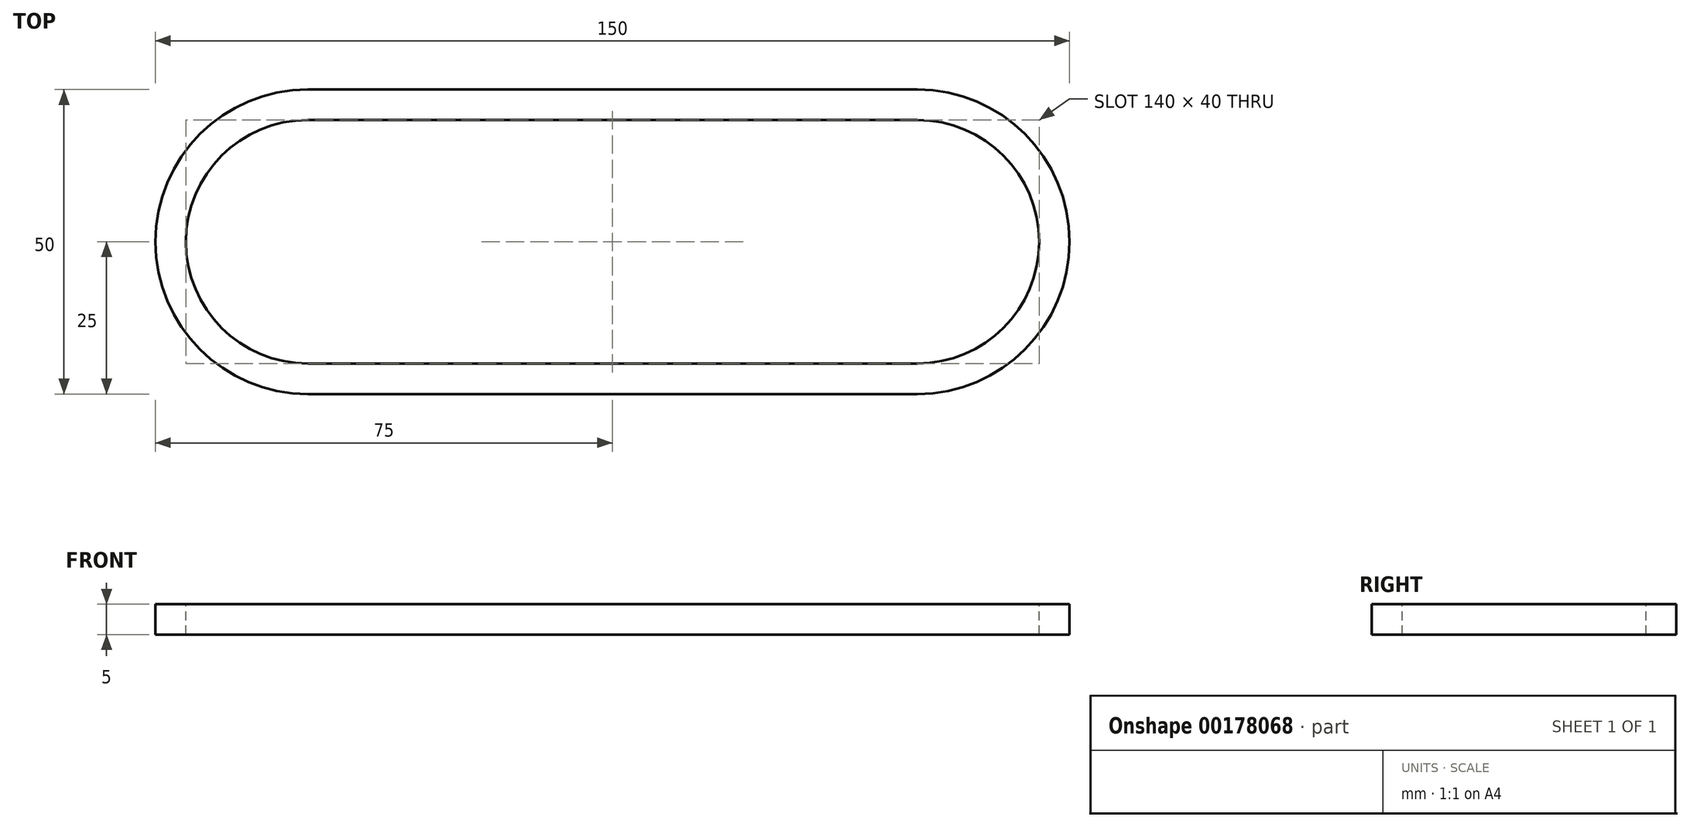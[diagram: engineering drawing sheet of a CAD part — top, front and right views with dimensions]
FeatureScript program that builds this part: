
annotation { "Feature Type Name" : "Feature", "Feature Type Description" : "" }
export const myFeature = defineFeature(function(context is Context, id is Id, definition is map)
    precondition{}
    {
        {
            var Q0;
            Q0=qCreatedBy(makeId("Top.planeOp"),FACE);
            var sketch = newSketch(context, id + "F0", { "sketchPlane" : qUnion([Q0])});
            skLineSegment(sketch, "E0", {"start": v(0, 0) * mm, "end": v(0, 25) * mm, "construction": true});
            skLineSegment(sketch, "E1", {"start": v(0, 0) * mm, "end": v(0, -25) * mm, "construction": true});
            skLineSegment(sketch, "E2", {"start": v(0, 25) * mm, "end": v(-50, 25) * mm});
            skLineSegment(sketch, "E3", {"start": v(0, -25) * mm, "end": v(-50, -25) * mm});
            skCircle(sketch, "E4", {"center": v(-50, 0) * mm, "radius": 25 * mm});
            skLineSegment(sketch, "E5.MirrorCS", {"start": v(0, 25) * mm, "end": v(50, 25) * mm});
            skCircle(sketch, "E6.MirrorC", {"center": v(50, 0) * mm, "radius": 25 * mm});
            skLineSegment(sketch, "E7.MirrorCS", {"start": v(0, -25) * mm, "end": v(50, -25) * mm});
            skSolve(sketch);
        }
        {
            var Q0;
            Q0 = qSketchRegion(id + "F0", true);
            extrude(context, id + "F1", {"entities" : qUnion([Q0]), "depth" : 5 * mm});
        }
        {
            var Q0;
            Q0=makeQuery(id+"F1.opExtrude","CAP_FACE",FACE,{"disambiguationData":[OSD([sQuery(id+"F0.wireOp",EDGE,"E2"),sQuery(id+"F0.wireOp",EDGE,"E3"),sQuery(id+"F0.wireOp",EDGE,"E4"),sQuery(id+"F0.wireOp",EDGE,"E5.MirrorCS"),sQuery(id+"F0.wireOp",EDGE,"E6.MirrorC"),sQuery(id+"F0.wireOp",EDGE,"E7.MirrorCS")])],"isStart":false});
            var sketch = newSketch(context, id + "F2", { "sketchPlane" : qUnion([Q0])});
            skLineSegment(sketch, "E8", {"start": v(0, 20) * mm, "end": v(0, -20) * mm, "construction": true});
            skLineSegment(sketch, "E9", {"start": v(0, 20) * mm, "end": v(-50, 20) * mm});
            skLineSegment(sketch, "E10", {"start": v(0, -20) * mm, "end": v(-50, -20) * mm});
            skCircle(sketch, "E11", {"center": v(-50, 0) * mm, "radius": 20 * mm});
            skLineSegment(sketch, "E12.MirrorCS", {"start": v(0, 20) * mm, "end": v(50, 20) * mm});
            skCircle(sketch, "E13.MirrorC", {"center": v(50, 0) * mm, "radius": 20 * mm});
            skLineSegment(sketch, "E14.MirrorCS", {"start": v(0, -20) * mm, "end": v(50, -20) * mm});
            skLineSegment(sketch, "E15", {"start": v(-50, 20) * mm, "end": v(-50, -20) * mm});
            skLineSegment(sketch, "E16", {"start": v(50, 20) * mm, "end": v(50, -20) * mm});
            skSolve(sketch);
        }
        {
            var Q0;
            Q0 = qSketchRegion(id + "F2", true);
            extrude(context, id + "F3", {"entities" : qUnion([Q0]), "operationType" : NewBodyOperationType.REMOVE, "oppositeDirection" : true, "depth" : 25 * mm});
        }
    });
